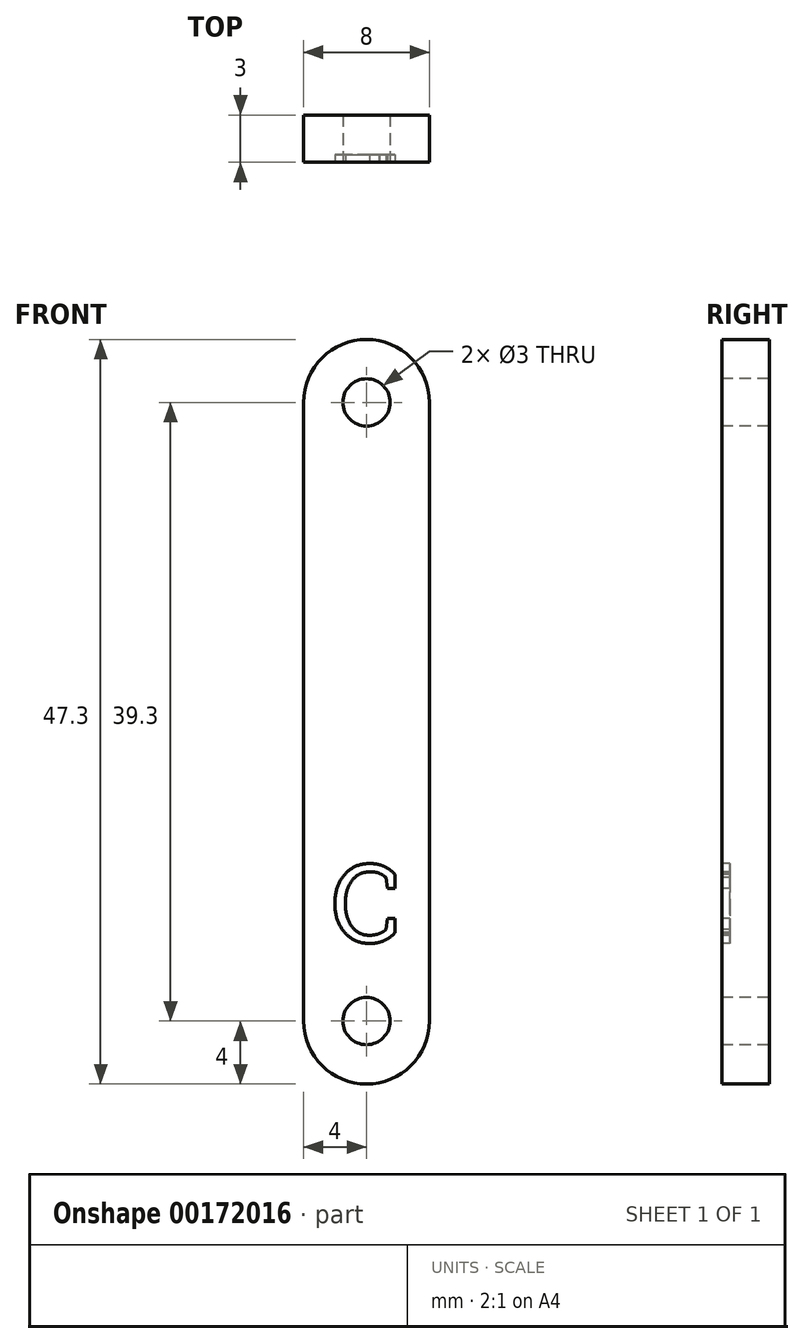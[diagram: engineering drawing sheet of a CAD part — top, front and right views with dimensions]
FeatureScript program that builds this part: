
annotation { "Feature Type Name" : "Feature", "Feature Type Description" : "" }
export const myFeature = defineFeature(function(context is Context, id is Id, definition is map)
    precondition{}
    {
        {
            assignVariable(context, id + "F0", {"name" : "Thickness", "anyValue" : 3});
        }
        {
            var Q0;
            Q0=qCreatedBy(makeId("Front.planeOp"),FACE);
            var sketch = newSketch(context, id + "F1", { "sketchPlane" : qUnion([Q0])});
            skCircle(sketch, "E0", {"center": v(0, 39.3) * mm, "radius": 1.5 * mm});
            skCircle(sketch, "E1", {"center": v(0, 0) * mm, "radius": 1.5 * mm});
            skArc(sketch, "E2", {"start": v(4, 39.3) * mm, "mid": v(0, 43.3) * mm, "end": v(-4, 39.3) * mm});
            skArc(sketch, "E3", {"start": v(-4, 0) * mm, "mid": v(0, -4) * mm, "end": v(4, 0) * mm});
            skLineSegment(sketch, "E4", {"start": v(-4, 0) * mm, "end": v(-4, 39.3) * mm});
            skLineSegment(sketch, "E5", {"start": v(4, 39.3) * mm, "end": v(4, 0) * mm});
            skSolve(sketch);
        }
        {
            var Q0;
            Q0=makeQuery(id+"F1.imprint","IMPRINT",FACE,{"disambiguationData":[TD([[makeQuery(id+"F1.imprint","IMPRINT",EDGE,{"derivedFrom":sQuery(id+"F1.wireOp",EDGE,"E0")}),-1.0]])]});
            extrude(context, id + "F2", {"entities" : qUnion([Q0]), "oppositeDirection" : true, "depth" : (getVariable(context, 'Thickness')) * mm});
        }
        {
            var Q0;
            Q0=qCreatedBy(makeId("Front.planeOp"),FACE);
            var sketch = newSketch(context, id + "F3", { "sketchPlane" : qUnion([Q0])});
            skText(sketch, "E6", { "text": "C", "fontName": "RobotoSlab-Regular.ttf"});
            skLineSegment(sketch, "E7", {"start": v(4, 19.65) * mm, "end": v(1.35, 19.65) * mm, "construction": true});
            const initialGuessF3  = {"E6": [-0.00225, 0.005, 1, 0, 0.005]};
            skSetInitialGuess(sketch, initialGuessF3);
            skSolve(sketch);
        }
        {
            assignVariable(context, id + "F4", {"name" : "DepthText", "anyValue" : .5});
        }
        {
            var Q0;
            Q0=qSketchRegion(id+"F3",true);
            extrude(context, id + "F5", {"entities" : qUnion([Q0]), "operationType" : NewBodyOperationType.REMOVE, "oppositeDirection" : true, "depth" : (getVariable(context, 'DepthText')) * mm});
        }
    });
